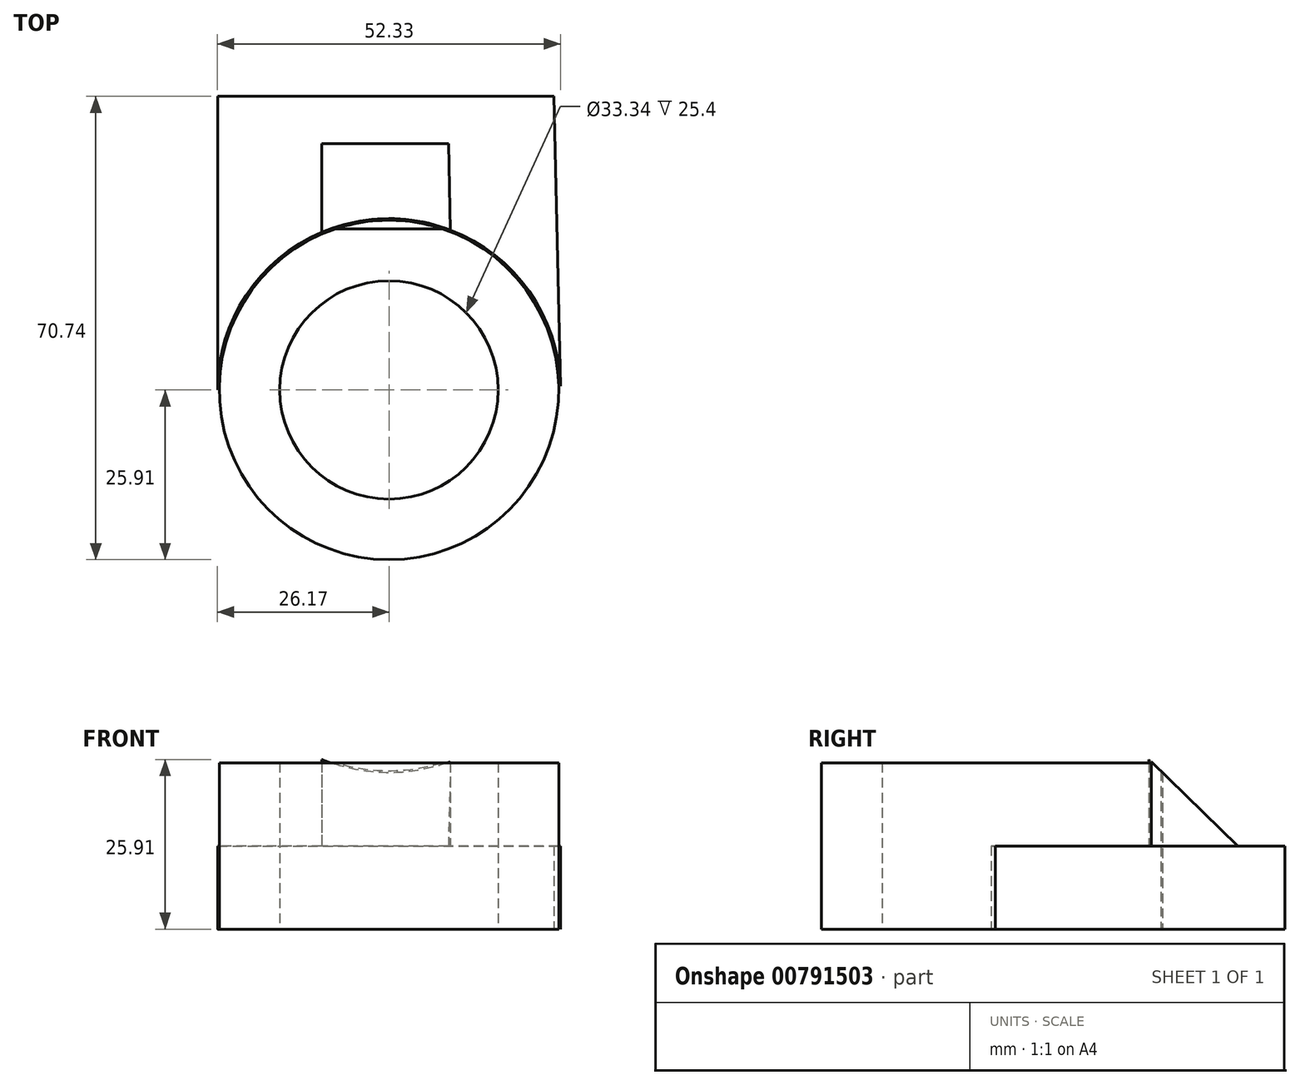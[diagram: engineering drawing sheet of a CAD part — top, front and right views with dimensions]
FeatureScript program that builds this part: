
annotation { "Feature Type Name" : "Feature", "Feature Type Description" : "" }
export const myFeature = defineFeature(function(context is Context, id is Id, definition is map)
    precondition{}
    {
        {
            var Q0;
            Q0=qCreatedBy(makeId("Top.planeOp"),FACE);
            var sketch = newSketch(context, id + "F0", { "sketchPlane" : qUnion([Q0])});
            skCircle(sketch, "E0", {"center": v(0, 0) * mm, "radius": 26.17 * mm});
            skCircle(sketch, "E1", {"center": v(0, 0) * mm, "radius": 18.78 * mm});
            skLineSegment(sketch, "E2", {"start": v(-26.17, 0) * mm, "end": v(-26.17, 44.83) * mm});
            skLineSegment(sketch, "E3", {"start": v(-26.17, 44.83) * mm, "end": v(25.15, 44.83) * mm});
            skLineSegment(sketch, "E4", {"start": v(25.15, 44.83) * mm, "end": v(26.18, 0) * mm});
            skSolve(sketch);
        }
        {
            var Q0;
            {var subQ0=sQuery(id+"F0.wireOp",EDGE,"E2");Q0=makeQuery(id+"F0.imprint","IMPRINT",FACE,{"disambiguationData":[TD([[makeQuery(id+"F0.imprint","IMPRINT",EDGE,{"derivedFrom":subQ0}),-1.0]])]});}
            extrude(context, id + "F1", {"entities" : qUnion([Q0]), "depth" : 12.7 * mm, "offsetDistance" : 25.4 * mm});
        }
        {
            var Q0;
            Q0=qCreatedBy(makeId("Top.planeOp"),FACE);
            var sketch = newSketch(context, id + "F2", { "sketchPlane" : qUnion([Q0])});
            skCircle(sketch, "E5", {"center": v(0, 0) * mm, "radius": 25.91 * mm});
            skCircle(sketch, "E6", {"center": v(0, 0) * mm, "radius": 16.67 * mm});
            skSolve(sketch);
        }
        {
            var Q0;
            Q0 = qSketchRegion(id + "F2", true);
            extrude(context, id + "F3", {"entities" : qUnion([Q0]), "depth" : 25.4 * mm, "offsetDistance" : 25.4 * mm});
        }
        {
            var Q0;
            Q0=makeQuery(id+"F1.opExtrude","CAP_FACE",FACE,{"disambiguationData":[OSD([sQuery(id+"F0.wireOp",EDGE,"E0"),sQuery(id+"F0.wireOp",EDGE,"E2"),sQuery(id+"F0.wireOp",EDGE,"E3"),sQuery(id+"F0.wireOp",EDGE,"E4")])],"isStart":false});
            var sketch = newSketch(context, id + "F4", { "sketchPlane" : qUnion([Q0])});
            skLineSegment(sketch, "E7", {"start": v(9.39, 24.43) * mm, "end": v(9.09, 37.61) * mm});
            skLineSegment(sketch, "E8", {"start": v(9.09, 37.61) * mm, "end": v(-10.26, 37.61) * mm});
            skLineSegment(sketch, "E9", {"start": v(-10.26, 37.61) * mm, "end": v(-10.26, 24.07) * mm});
            skSolve(sketch);
        }
        {
            var Q0;
            Q0 = qSketchRegion(id + "F4", true);
            var Q1;
            {var subQ0=sQuery(id+"F4.wireOp",EDGE,"E7");Q1=makeQuery(id+"F4.imprint","IMPRINT",FACE,{"disambiguationData":[TD([[makeQuery(id+"F4.imprint","IMPRINT",EDGE,{"derivedFrom":subQ0}),1.0]])]});}
            extrude(context, id + "F5", {"entities" : qUnion([Q0, Q1]), "operationType" : NewBodyOperationType.ADD, "depth" : 13.2 * mm, "offsetDistance" : 25.4 * mm});
        }
        {
            var Q0;
            Q0=makeQuery(id+"F5.opExtrude","SWEPT_FACE",FACE,{"disambiguationData":[OSD([sQuery(id+"F4.wireOp",EDGE,"E9")])]});
            var sketch = newSketch(context, id + "F6", { "sketchPlane" : qUnion([Q0])});
            skLineSegment(sketch, "E10", {"start": v(-24.07, 25.9) * mm, "end": v(-37.61, 12.7) * mm});
            skSolve(sketch);
        }
        {
            var Q0;
            Q0=makeQuery(id+"F6.imprint","IMPRINT",FACE,{"disambiguationData":[TD([[makeQuery(id+"F6.imprint","IMPRINT",EDGE,{"derivedFrom":sQuery(id+"F6.wireOp",EDGE,"E10")}),-1.0]])]});
            extrude(context, id + "F7", {"entities" : qUnion([Q0]), "operationType" : NewBodyOperationType.REMOVE, "oppositeDirection" : true, "depth" : 25.4 * mm, "offsetDistance" : 25.4 * mm});
        }
        {
            var Q0;
            Q0=makeQuery(id+"F6.imprint","IMPRINT",FACE,{"disambiguationData":[TD([[makeQuery(id+"F6.imprint","IMPRINT",EDGE,{"derivedFrom":sQuery(id+"F6.wireOp",EDGE,"E10")}),-1.0]])]});
            var sketch = newSketch(context, id + "F8", { "sketchPlane" : qUnion([Q0])});
            skSolve(sketch);
        }
        {
            var Q0;
            Q0=makeQuery(id+"F8.imprint","IMPRINT",FACE,{"disambiguationData":[TD([[makeQuery(id+"F8.imprint","IMPRINT",EDGE,{"derivedFrom":makeQuery(id+"F6.imprint","IMPRINT",EDGE,{"derivedFrom":sQuery(id+"F6.wireOp",EDGE,"E10")})}),-1.0]])]});
            extrude(context, id + "F9", {"entities" : qUnion([Q0]), "operationType" : NewBodyOperationType.REMOVE, "oppositeDirection" : true, "depth" : 25.4 * mm, "offsetDistance" : 25.4 * mm});
        }
    });
